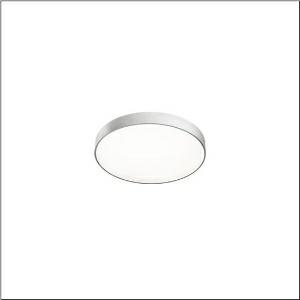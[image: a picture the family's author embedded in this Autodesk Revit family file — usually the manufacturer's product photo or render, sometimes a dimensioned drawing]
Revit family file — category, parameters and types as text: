
# Revit family: round_21_s_51mr34fd0321s
name_source: partatom
category: Lighting Fixtures
units: mm (PartAtom-declared; Revit-internal decimal feet)

## family parameters
Cut with Voids When Loaded = No
Host = Face
Light Source = No
Part Type = Normal
Room Calculation Point = No
Round Connector Dimension = Use Diameter
Shared = No

## types (1)
- Round 21 S (1 x LED, 3750 lm, 30.3 W, 3000K)
    Apparent Load = 30 VA
    CIE Flux Codes = 49 80 96 100 100
    Color Rendering = 80
    Color Temperature = 3000K
    Default Elevation = 1800 mm
    Description = Round 21 S, wall and ceiling luminaire, primary optical cover: cover, of PMMA, opal, light emission: direct distribution, primary light characteristic: symmetric, installation type: suspended mounting, surface-mounted, LED, rated luminous flux: 3.750lm, luminous efficacy: 124lm/W, light colour: 830, colour temperature: 3000K, control gear: DALI 2, with terminal, 5-pole, mains connection: 230V, AC, 50/60Hz, rated input power: 30.3W, housing, of aluminium, coated, silver, diameter: 400mm, height: 62mm, protection rating (complete): IP40, insulation class (complete): insulation class I (protective earthing), certification: CE, impact resistance: IK04, permissible operating ambient temperature: -10..+35°C, packaging unit: 1 piece
    Height = 87 mm
    Lamp = 1 x LED
    Lamp Light Flux = 3750 lm
    Lamp Power = 30.3 W
    Lamp count = 1
    Length = 400 mm
    Luminous efficacy = 124 lm/W
    Manufacturer = Siteco
    ModVariant = No
    Model = 51MR34FD0321S
    Mounting Place = Ceiling
    Mounting Type = Surface mounted
    Number of Poles = 1
    OnlyDefault = Yes
    Power Factor = 1
    Product Name = Round 21 S
    Product group = wall and ceiling luminaire | ceiling mounted
    ProductGroupID = 304
    Protection Class = Protection class I
    Protection Degree = IP 40
    RLX_Detail_Level = 1
    RLX_Emergency_Light_Flux = 0 lm
    RLX_Emergency_Type = 0
    RLX_Emergency_Type_DB = No
    RlxData = <blob elided: 11173 chars, md5=ff77212d>
    Socket = socket
    Standby Power = 0 W
    System Light Flux = 3750 lm
    System Power = 30 W
    Type Comments = Product without accessories
    Type Image = l_1258309.jpg
    URL = http://relux.com
    VarID = ---
    Voltage = 0 V
    Weight = 0.00 kg
    Width = 0 mm  [stored 0 ft]

note: [stored X ft] marks values corroborated as IEEE doubles in the binary element streams (Revit-internal decimal feet)

## geometry (parser evidence)
native form markers: Sweep x8
no freeform markers — native parametric forms only
